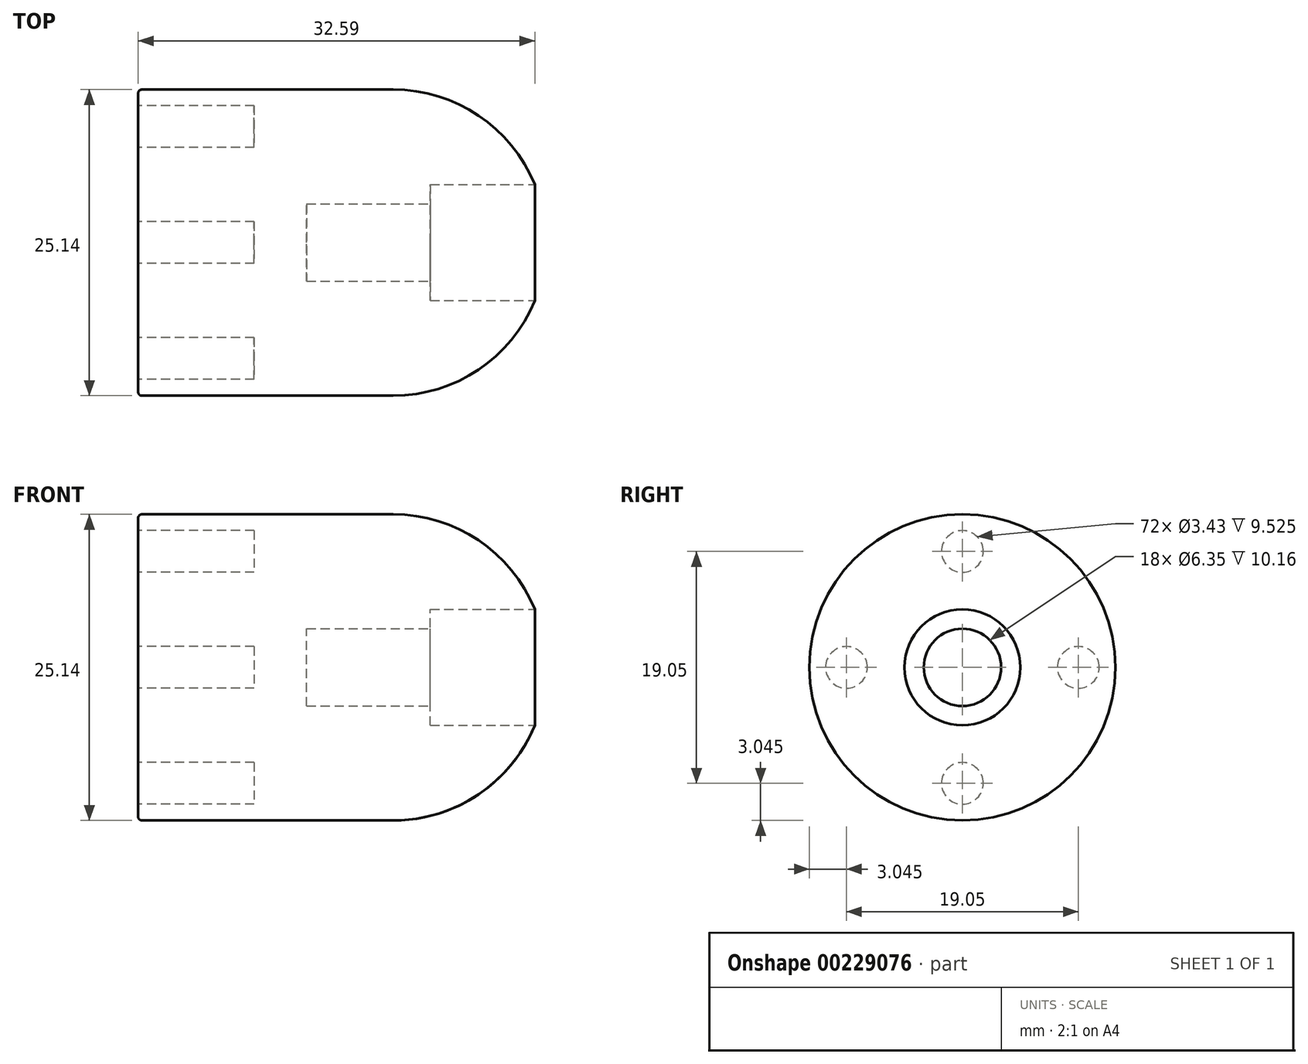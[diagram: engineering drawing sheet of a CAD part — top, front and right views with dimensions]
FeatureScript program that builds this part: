
annotation { "Feature Type Name" : "Feature", "Feature Type Description" : "" }
export const myFeature = defineFeature(function(context is Context, id is Id, definition is map)
    precondition{}
    {
        {
            var Q0;
            Q0=qCreatedBy(makeId("Front.planeOp"),FACE);
            var sketch = newSketch(context, id + "F0", { "sketchPlane" : qUnion([Q0])});
            skLineSegment(sketch, "E0", {"start": v(0, 0) * mm, "end": v(0, 12.57) * mm});
            skLineSegment(sketch, "E1", {"start": v(0, 12.57) * mm, "end": v(20.96, 12.57) * mm});
            skLineSegment(sketch, "E2", {"start": v(32.6, 4.76) * mm, "end": v(24, 4.76) * mm});
            skLineSegment(sketch, "E3", {"start": v(24, 4.76) * mm, "end": v(24, 3.18) * mm});
            skLineSegment(sketch, "E4", {"start": v(24, 3.18) * mm, "end": v(13.84, 3.18) * mm});
            skLineSegment(sketch, "E5", {"start": v(13.84, 3.18) * mm, "end": v(13.84, 0) * mm});
            skLineSegment(sketch, "E6", {"start": v(13.84, 0) * mm, "end": v(0, 0) * mm});
            skArc(sketch, "E7", {"start": v(32.6, 4.76) * mm, "mid": v(27.96, 10.44) * mm, "end": v(20.96, 12.57) * mm});
            skPoint(sketch, "E8.orphan", {"position": v(33.53, 0) * mm});
            skPoint(sketch, "E9.end.orphan", {"position": v(24, 2.38) * mm});
            skPoint(sketch, "E10.orphan", {"position": v(24, 0) * mm});
            skSolve(sketch);
        }
        {
            var Q0;
            Q0 = qSketchRegion(id + "F0", true);
            var Q1;
            Q1=sQuery(id+"F0.wireOp",EDGE,"E6");
            revolve(context, id + "F1", {"entities" : qUnion([Q0]), "axis" : qUnion([Q1]), "revolveType" : RevolveType.FULL});
        }
        {
            var Q0;
            Q0=makeQuery(id+"F1.opRevolve","SWEPT_FACE",FACE,{"disambiguationData":[OSD([sQuery(id+"F0.wireOp",EDGE,"E0")])]});
            var sketch = newSketch(context, id + "F2", { "sketchPlane" : qUnion([Q0])});
            skCircle(sketch, "E11", {"center": v(0, 9.53) * mm, "radius": 1.71 * mm});
            skCircle(sketch, "E12", {"center": v(-9.53, 0) * mm, "radius": 1.71 * mm});
            skCircle(sketch, "E13", {"center": v(0, -9.53) * mm, "radius": 1.71 * mm});
            skCircle(sketch, "E14", {"center": v(9.53, 0) * mm, "radius": 1.71 * mm});
            skSolve(sketch);
        }
        {
            var Q0;
            Q0 = qSketchRegion(id + "F2", true);
            extrude(context, id + "F3", {"entities" : qUnion([Q0]), "operationType" : NewBodyOperationType.REMOVE, "oppositeDirection" : true, "depth" : 9.52 * mm});
        }
        {
            var Q0;
            Q0=makeQuery(id+"F1.opRevolve","SWEPT_EDGE",EDGE,{"disambiguationData":[OSD([sQuery(id+"F0.wireOp",EDGE,"E0"),sQuery(id+"F0.wireOp",EDGE,"E1")])]});
            fillet(context, id + "F4", {"entities" : qUnion([Q0]), "radius" : 0.3 * mm, "tangentPropagation" : true, "allowEdgeOverflow" : false});
        }
    });
